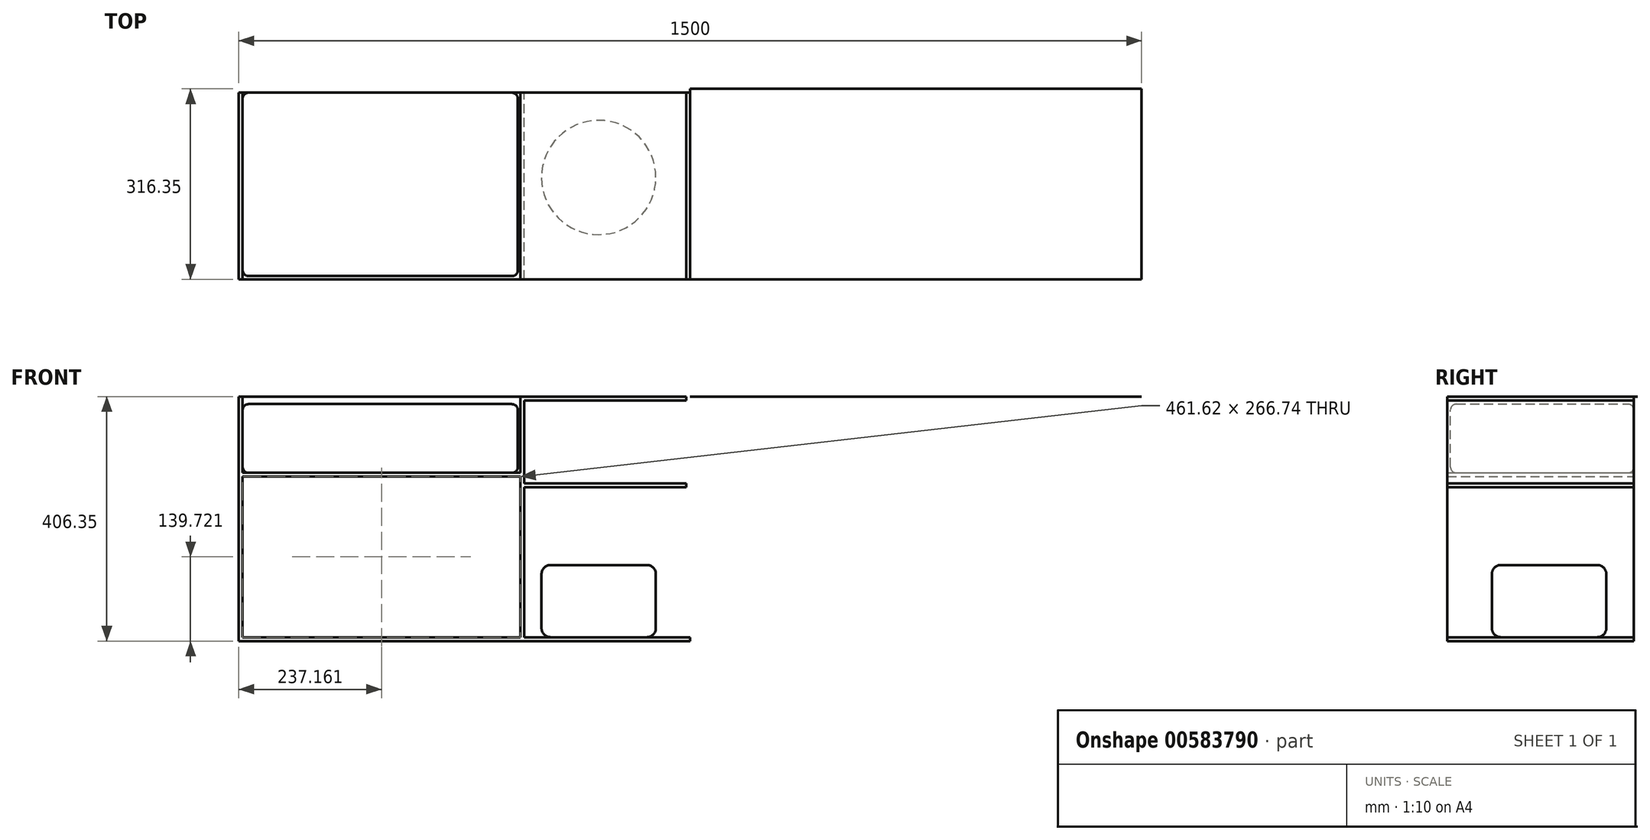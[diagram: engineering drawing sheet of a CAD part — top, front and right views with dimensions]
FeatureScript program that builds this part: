
annotation { "Feature Type Name" : "Feature", "Feature Type Description" : "" }
export const myFeature = defineFeature(function(context is Context, id is Id, definition is map)
    precondition{}
    {
        {
            var Q0;
            Q0=qCreatedBy(makeId("Front.planeOp"),FACE);
            var sketch = newSketch(context, id + "F0", { "sketchPlane" : qUnion([Q0])});
            skLineSegment(sketch, "E0", {"start": v(0, 0) * mm, "end": v(457.2, 0) * mm});
            skLineSegment(sketch, "E1", {"start": v(457.2, 0) * mm, "end": v(457.2, 114.3) * mm});
            skLineSegment(sketch, "E2", {"start": v(457.2, 114.3) * mm, "end": v(0, 114.3) * mm});
            skLineSegment(sketch, "E3", {"start": v(0, 114.3) * mm, "end": v(0, 0) * mm});
            skSolve(sketch);
        }
        {
            var Q0;
            Q0=makeQuery(id+"F0.imprint","IMPRINT",FACE,{"disambiguationData":[TD([[makeQuery(id+"F0.imprint","IMPRINT",EDGE,{"derivedFrom":sQuery(id+"F0.wireOp",EDGE,"E0")}),1.0]])]});
            extrude(context, id + "F1", {"entities" : qUnion([Q0]), "depth" : 304.8 * mm, "offsetDistance" : 25 * mm});
        }
        {
            var Q0;
            Q0=makeQuery(id+"F1.opExtrude","CAP_EDGE",EDGE,{"disambiguationData":[OSD([sQuery(id+"F0.wireOp",EDGE,"E2")])],"isStart":false});
            var Q1;
            Q1=makeQuery(id+"F1.opExtrude","CAP_EDGE",EDGE,{"disambiguationData":[OSD([sQuery(id+"F0.wireOp",EDGE,"E3")])],"isStart":false});
            var Q2;
            Q2=makeQuery(id+"F1.opExtrude","CAP_EDGE",EDGE,{"disambiguationData":[OSD([sQuery(id+"F0.wireOp",EDGE,"E0")])],"isStart":false});
            var Q3;
            Q3=makeQuery(id+"F1.opExtrude","CAP_EDGE",EDGE,{"disambiguationData":[OSD([sQuery(id+"F0.wireOp",EDGE,"E1")])],"isStart":false});
            var Q4;
            Q4=makeQuery(id+"F1.opExtrude","SWEPT_EDGE",EDGE,{"disambiguationData":[OSD([sQuery(id+"F0.wireOp",EDGE,"E1"),sQuery(id+"F0.wireOp",EDGE,"E2")])]});
            var Q5;
            Q5=makeQuery(id+"F1.opExtrude","CAP_EDGE",EDGE,{"disambiguationData":[OSD([sQuery(id+"F0.wireOp",EDGE,"E1")])],"isStart":true});
            var Q6;
            Q6=makeQuery(id+"F1.opExtrude","SWEPT_EDGE",EDGE,{"disambiguationData":[OSD([sQuery(id+"F0.wireOp",EDGE,"E0"),sQuery(id+"F0.wireOp",EDGE,"E1")])]});
            var Q7;
            Q7=makeQuery(id+"F1.opExtrude","CAP_EDGE",EDGE,{"disambiguationData":[OSD([sQuery(id+"F0.wireOp",EDGE,"E2")])],"isStart":true});
            var Q8;
            Q8=makeQuery(id+"F1.opExtrude","SWEPT_EDGE",EDGE,{"disambiguationData":[OSD([sQuery(id+"F0.wireOp",EDGE,"E2"),sQuery(id+"F0.wireOp",EDGE,"E3")])]});
            var Q9;
            Q9=makeQuery(id+"F1.opExtrude","SWEPT_EDGE",EDGE,{"disambiguationData":[OSD([sQuery(id+"F0.wireOp",EDGE,"E0"),sQuery(id+"F0.wireOp",EDGE,"E3")])]});
            var Q10;
            Q10=makeQuery(id+"F1.opExtrude","CAP_EDGE",EDGE,{"disambiguationData":[OSD([sQuery(id+"F0.wireOp",EDGE,"E3")])],"isStart":true});
            var Q11;
            Q11=makeQuery(id+"F1.opExtrude","CAP_EDGE",EDGE,{"disambiguationData":[OSD([sQuery(id+"F0.wireOp",EDGE,"E0")])],"isStart":true});
            fillet(context, id + "F2", {"entities" : qUnion([Q0, Q1, Q2, Q3, Q4, Q5, Q6, Q7, Q8, Q9, Q10, Q11]), "radius" : 10 * mm, "tangentPropagation" : true, "allowEdgeOverflow" : false});
        }
        {
            var Q0;
            Q0=qCreatedBy(makeId("Front.planeOp"),FACE);
            var sketch = newSketch(context, id + "F3", { "sketchPlane" : qUnion([Q0])});
            skLineSegment(sketch, "E4.bottom", {"start": v(-6.35, 126.91) * mm, "end": v(0, 126.91) * mm});
            skLineSegment(sketch, "E4.top", {"start": v(-6.35, -273.09) * mm, "end": v(0, -273.09) * mm});
            skLineSegment(sketch, "E4.left", {"start": v(-6.35, 126.91) * mm, "end": v(-6.35, -273.09) * mm});
            skLineSegment(sketch, "E4.right", {"start": v(0, 126.91) * mm, "end": v(0, -273.09) * mm});
            skLineSegment(sketch, "E5.bottom", {"start": v(-6.35, -273.09) * mm, "end": v(743.65, -273.09) * mm});
            skLineSegment(sketch, "E5.top", {"start": v(-6.35, -279.44) * mm, "end": v(743.65, -279.44) * mm});
            skLineSegment(sketch, "E5.left", {"start": v(-6.35, -273.09) * mm, "end": v(-6.35, -279.44) * mm});
            skLineSegment(sketch, "E5.right", {"start": v(743.65, -273.09) * mm, "end": v(743.65, -279.44) * mm});
            skLineSegment(sketch, "E6.bottom", {"start": v(743.65, -273.09) * mm, "end": v(737.3, -273.09) * mm});
            skLineSegment(sketch, "E6.top", {"start": v(743.65, 126.91) * mm, "end": v(737.3, 126.91) * mm});
            skLineSegment(sketch, "E6.left", {"start": v(743.65, -273.09) * mm, "end": v(743.65, 126.91) * mm});
            skLineSegment(sketch, "E6.right", {"start": v(737.3, -273.09) * mm, "end": v(737.3, 126.91) * mm});
            skLineSegment(sketch, "E7.bottom", {"start": v(461.62, 126.91) * mm, "end": v(467.97, 126.91) * mm});
            skLineSegment(sketch, "E7.top", {"start": v(461.62, -273.09) * mm, "end": v(467.97, -273.09) * mm});
            skLineSegment(sketch, "E7.left", {"start": v(461.62, 126.91) * mm, "end": v(461.62, -273.09) * mm});
            skLineSegment(sketch, "E7.right", {"start": v(467.97, 126.91) * mm, "end": v(467.97, -273.09) * mm});
            skLineSegment(sketch, "E8.bottom", {"start": v(0, 0) * mm, "end": v(461.62, 0) * mm});
            skLineSegment(sketch, "E8.top", {"start": v(0, -6.35) * mm, "end": v(461.62, -6.35) * mm});
            skLineSegment(sketch, "E8.left", {"start": v(0, 0) * mm, "end": v(0, -6.35) * mm});
            skLineSegment(sketch, "E8.right", {"start": v(461.62, 0) * mm, "end": v(461.62, -6.35) * mm});
            skLineSegment(sketch, "E9.bottom", {"start": v(467.97, 126.91) * mm, "end": v(737.3, 126.91) * mm});
            skLineSegment(sketch, "E9.top", {"start": v(467.97, 120.56) * mm, "end": v(737.3, 120.56) * mm});
            skLineSegment(sketch, "E9.left", {"start": v(467.97, 126.91) * mm, "end": v(467.97, 120.56) * mm});
            skLineSegment(sketch, "E9.right", {"start": v(737.3, 126.91) * mm, "end": v(737.3, 120.56) * mm});
            skLineSegment(sketch, "E10.bottom", {"start": v(467.97, -17.26) * mm, "end": v(737.3, -17.26) * mm});
            skLineSegment(sketch, "E10.top", {"start": v(467.97, -23.6) * mm, "end": v(737.3, -23.6) * mm});
            skLineSegment(sketch, "E10.left", {"start": v(467.97, -17.26) * mm, "end": v(467.97, -23.6) * mm});
            skLineSegment(sketch, "E10.right", {"start": v(737.3, -17.26) * mm, "end": v(737.3, -23.6) * mm});
            skSolve(sketch);
        }
        {
            var Q0;
            Q0=makeQuery(id+"F3.imprint","IMPRINT",FACE,{"disambiguationData":[TD([[makeQuery(id+"F3.imprint","IMPRINT",EDGE,{"derivedFrom":sQuery(id+"F3.wireOp",EDGE,"E4.bottom")}),-1.0]])]});
            var Q1;
            Q1=makeQuery(id+"F3.imprint","IMPRINT",FACE,{"disambiguationData":[TD([[makeQuery(id+"F3.imprint","IMPRINT",EDGE,{"derivedFrom":sQuery(id+"F3.wireOp",EDGE,"E5.top")}),1.0]])]});
            var Q2;
            Q2=makeQuery(id+"F3.imprint","IMPRINT",FACE,{"disambiguationData":[TD([[makeQuery(id+"F3.imprint","IMPRINT",EDGE,{"derivedFrom":sQuery(id+"F3.wireOp",EDGE,"E6.bottom")}),-1.0]])]});
            var Q3;
            Q3=makeQuery(id+"F3.imprint","IMPRINT",FACE,{"disambiguationData":[TD([[makeQuery(id+"F3.imprint","IMPRINT",EDGE,{"derivedFrom":sQuery(id+"F3.wireOp",EDGE,"E7.bottom")}),-1.0]])]});
            var Q4;
            Q4=makeQuery(id+"F3.imprint","IMPRINT",FACE,{"disambiguationData":[TD([[makeQuery(id+"F3.imprint","IMPRINT",EDGE,{"derivedFrom":sQuery(id+"F3.wireOp",EDGE,"E8.bottom")}),-1.0]])]});
            var Q5;
            Q5=makeQuery(id+"F3.imprint","IMPRINT",FACE,{"disambiguationData":[TD([[makeQuery(id+"F3.imprint","IMPRINT",EDGE,{"derivedFrom":sQuery(id+"F3.wireOp",EDGE,"E10.bottom")}),-1.0]])]});
            var Q6;
            Q6=makeQuery(id+"F3.imprint","IMPRINT",FACE,{"disambiguationData":[TD([[makeQuery(id+"F3.imprint","IMPRINT",EDGE,{"derivedFrom":sQuery(id+"F3.wireOp",EDGE,"E9.bottom")}),-1.0]])]});
            extrude(context, id + "F4", {"entities" : qUnion([Q0, Q1, Q2, Q3, Q4, Q5, Q6]), "depth" : 310 * mm, "offsetDistance" : 25 * mm});
        }
        {
            var Q0;
            Q0=makeQuery(id+"F4.opExtrude","CAP_FACE",FACE,{"disambiguationData":[OSD([sQuery(id+"F3.wireOp",EDGE,"E4.bottom"),sQuery(id+"F3.wireOp",EDGE,"E4.left"),sQuery(id+"F3.wireOp",EDGE,"E4.right"),sQuery(id+"F3.wireOp",EDGE,"E5.bottom"),sQuery(id+"F3.wireOp",EDGE,"E5.top"),sQuery(id+"F3.wireOp",EDGE,"E5.left"),sQuery(id+"F3.wireOp",EDGE,"E5.right"),sQuery(id+"F3.wireOp",EDGE,"E6.top"),sQuery(id+"F3.wireOp",EDGE,"E6.left"),sQuery(id+"F3.wireOp",EDGE,"E6.right"),sQuery(id+"F3.wireOp",EDGE,"E7.bottom"),sQuery(id+"F3.wireOp",EDGE,"E7.left"),sQuery(id+"F3.wireOp",EDGE,"E7.right")])],"isStart":true});
            var sketch = newSketch(context, id + "F5", { "sketchPlane" : qUnion([Q0])});
            skLineSegment(sketch, "E11.bottom", {"start": v(-743.65, 126.91) * mm, "end": v(6.35, 126.91) * mm});
            skLineSegment(sketch, "E11.top", {"start": v(-743.65, -279.44) * mm, "end": v(6.35, -279.44) * mm});
            skLineSegment(sketch, "E11.left", {"start": v(-743.65, 126.91) * mm, "end": v(-743.65, -279.44) * mm});
            skLineSegment(sketch, "E11.right", {"start": v(6.35, 126.91) * mm, "end": v(6.35, -279.44) * mm});
            skSolve(sketch);
        }
        {
            var Q0;
            Q0=makeQuery(id+"F5.imprint","IMPRINT",FACE,{"disambiguationData":[TD([[makeQuery(id+"F5.imprint","IMPRINT",EDGE,{"derivedFrom":sQuery(id+"F5.wireOp",EDGE,"E11.top")}),-1.0]])]});
            var Q1;
            {var subQ1=sQuery(id+"F3.wireOp",EDGE,"E6.right");var subQ2=makeQuery(id+"F4.opExtrude","CAP_EDGE",EDGE,{"disambiguationData":[OSD([subQ1])],"isStart":true});Q1=makeQuery(id+"F5.imprint","IMPRINT",FACE,{"disambiguationData":[TD([[makeQuery(id+"F5.imprint","IMPRINT",EDGE,{"derivedFrom":subQ2}),-1.0]])]});}
            var Q2;
            {var subQ1=sQuery(id+"F3.wireOp",EDGE,"E4.right");var subQ2=makeQuery(id+"F4.opExtrude","CAP_EDGE",EDGE,{"disambiguationData":[OSD([subQ1])],"isStart":true});Q2=makeQuery(id+"F5.imprint","IMPRINT",FACE,{"disambiguationData":[TD([[makeQuery(id+"F5.imprint","IMPRINT",EDGE,{"derivedFrom":subQ2}),-1.0]])]});}
            extrude(context, id + "F6", {"entities" : qUnion([Q0, Q1, Q2]), "depth" : 1 / 101.6 * mm, "offsetDistance" : 25 * mm});
        }
        {
            var Q0;
            {var subQ0=sQuery(id+"F3.wireOp",EDGE,"E5.bottom");Q0=makeQuery(id+"F4.opExtrude","SWEPT_FACE",FACE,{"disambiguationData":[OSD([subQ0]),TDD([makeQuery(id+"F3.imprint","IMPRINT",EDGE,{"disambiguationData":[TD([[makeQuery(id+"F3.imprint","INTERSECT",VERTEX,{"derivedFrom":[subQ0,sQuery(id+"F3.wireOp",EDGE,"E6.bottom"),sQuery(id+"F3.wireOp",EDGE,"E6.right")]}),1.0]])],"derivedFrom":subQ0})])]});}
            var sketch = newSketch(context, id + "F7", { "sketchPlane" : qUnion([Q0])});
            skCircle(sketch, "E12", {"center": v(591.6, -140.94) * mm, "radius": 95 * mm});
            skSolve(sketch);
        }
        {
            var Q0;
            Q0=makeQuery(id+"F7.imprint","IMPRINT",FACE,{"disambiguationData":[TD([[makeQuery(id+"F7.imprint","IMPRINT",EDGE,{"derivedFrom":sQuery(id+"F7.wireOp",EDGE,"E12")}),1.0]])]});
            extrude(context, id + "F8", {"entities" : qUnion([Q0]), "depth" : 120 * mm, "offsetDistance" : 25 * mm});
        }
        {
            var Q0;
            Q0=makeQuery(id+"F8.opExtrude","CAP_EDGE",EDGE,{"disambiguationData":[OSD([sQuery(id+"F7.wireOp",EDGE,"E12")])],"isStart":false});
            var Q1;
            Q1=makeQuery(id+"F8.opExtrude","CAP_EDGE",EDGE,{"disambiguationData":[OSD([sQuery(id+"F7.wireOp",EDGE,"E12")])],"isStart":true});
            fillet(context, id + "F9", {"entities" : qUnion([Q0, Q1]), "radius" : 15 * mm, "tangentPropagation" : true, "allowEdgeOverflow" : false});
        }
        {
            var Q0;
            Q0=makeQuery(id+"F4.opExtrude","SWEPT_FACE",FACE,{"disambiguationData":[OSD([sQuery(id+"F3.wireOp",EDGE,"E6.top"),sQuery(id+"F3.wireOp",EDGE,"E7.bottom"),sQuery(id+"F3.wireOp",EDGE,"E9.bottom")])]});
            var sketch = newSketch(context, id + "F10", { "sketchPlane" : qUnion([Q0])});
            skLineSegment(sketch, "E13.bottom", {"start": v(743.65, 6.35) * mm, "end": v(1493.65, 6.35) * mm});
            skLineSegment(sketch, "E13.top", {"start": v(743.65, -310) * mm, "end": v(1493.65, -310) * mm});
            skLineSegment(sketch, "E13.left", {"start": v(743.65, 6.35) * mm, "end": v(743.65, -310) * mm});
            skLineSegment(sketch, "E13.right", {"start": v(1493.65, 6.35) * mm, "end": v(1493.65, -310) * mm});
            skSolve(sketch);
        }
        {
            var Q0;
            {var subQ6=sQuery(id+"F10.wireOp",EDGE,"E13.bottom");Q0=makeQuery(id+"F10.imprint","IMPRINT",FACE,{"disambiguationData":[TD([[makeQuery(id+"F10.imprint","IMPRINT",EDGE,{"derivedFrom":subQ6}),-1.0]])]});}
            extrude(context, id + "F11", {"entities" : qUnion([Q0]), "oppositeDirection" : true, "depth" : 1 / 101.6 * mm, "offsetDistance" : 25 * mm});
        }
    });
